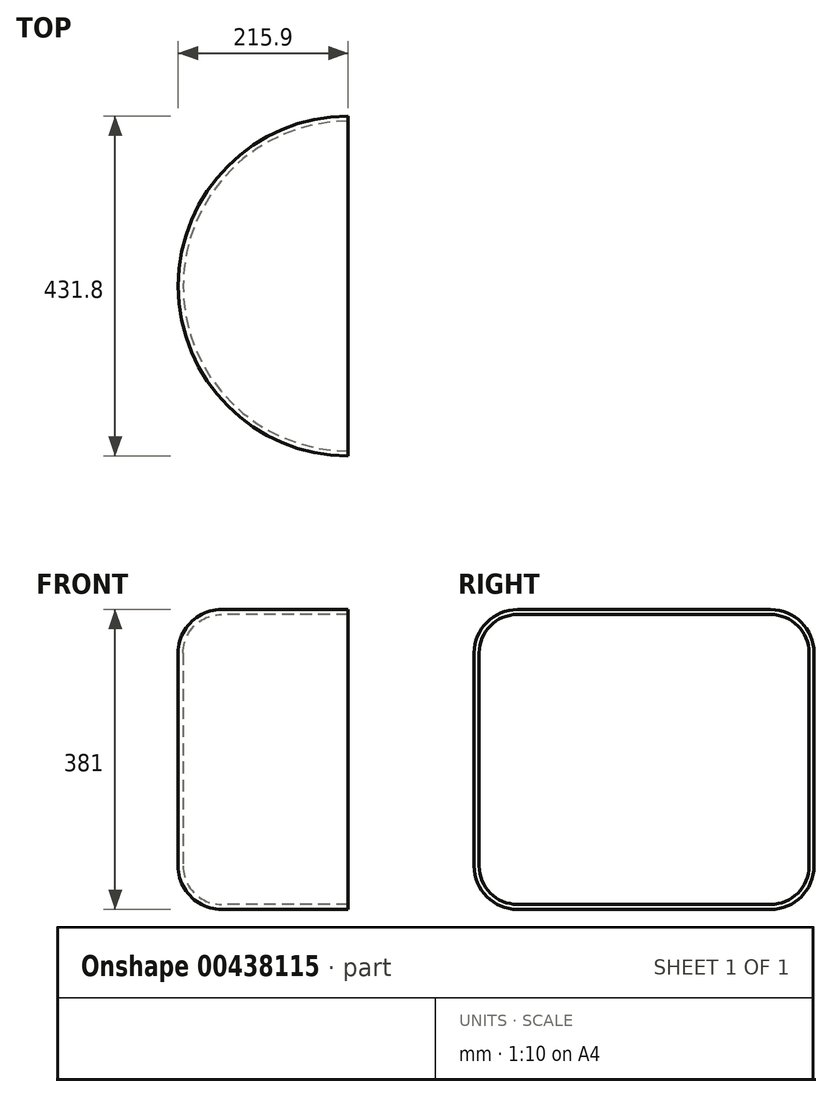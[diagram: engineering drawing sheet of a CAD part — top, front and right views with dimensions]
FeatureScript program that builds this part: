
annotation { "Feature Type Name" : "Feature", "Feature Type Description" : "" }
export const myFeature = defineFeature(function(context is Context, id is Id, definition is map)
    precondition{}
    {
        {
            var Q0;
            Q0=qCreatedBy(makeId("Top.planeOp"),FACE);
            var sketch = newSketch(context, id + "F0", { "sketchPlane" : qUnion([Q0])});
            skArc(sketch, "E0", {"start": v(0, 215.9) * mm, "mid": v(-215.9, 0) * mm, "end": v(0, -215.9) * mm});
            skLineSegment(sketch, "E1", {"start": v(0, 215.9) * mm, "end": v(0, -215.9) * mm});
            skSolve(sketch);
        }
        {
            var Q0;
            Q0=makeQuery(id+"F0.imprint","IMPRINT",FACE,{"disambiguationData":[TD([[makeQuery(id+"F0.imprint","IMPRINT",EDGE,{"derivedFrom":sQuery(id+"F0.wireOp",EDGE,"E0")}),1.0]])]});
            extrude(context, id + "F1", {"entities" : qUnion([Q0]), "depth" : 381 * mm});
        }
        {
            var Q0;
            Q0=makeQuery(id+"F1.opExtrude","CAP_EDGE",EDGE,{"disambiguationData":[OSD([sQuery(id+"F0.wireOp",EDGE,"E0")])],"isStart":false});
            fillet(context, id + "F2", {"entities" : qUnion([Q0]), "radius" : 55.2 * mm, "tangentPropagation" : true, "allowEdgeOverflow" : false});
        }
        {
            var Q0;
            Q0=makeQuery(id+"F1.opExtrude","CAP_EDGE",EDGE,{"disambiguationData":[OSD([sQuery(id+"F0.wireOp",EDGE,"E0")])],"isStart":true});
            fillet(context, id + "F3", {"entities" : qUnion([Q0]), "radius" : 55.2 * mm, "tangentPropagation" : true, "allowEdgeOverflow" : false});
        }
        {
            var Q0;
            Q0=makeQuery(id+"F1.opExtrude","SWEPT_FACE",FACE,{"disambiguationData":[OSD([sQuery(id+"F0.wireOp",EDGE,"E1")])]});
            shell(context, id + "F4", {"entities" : qUnion([Q0]), "thickness" : 6.35 * mm});
        }
    });
